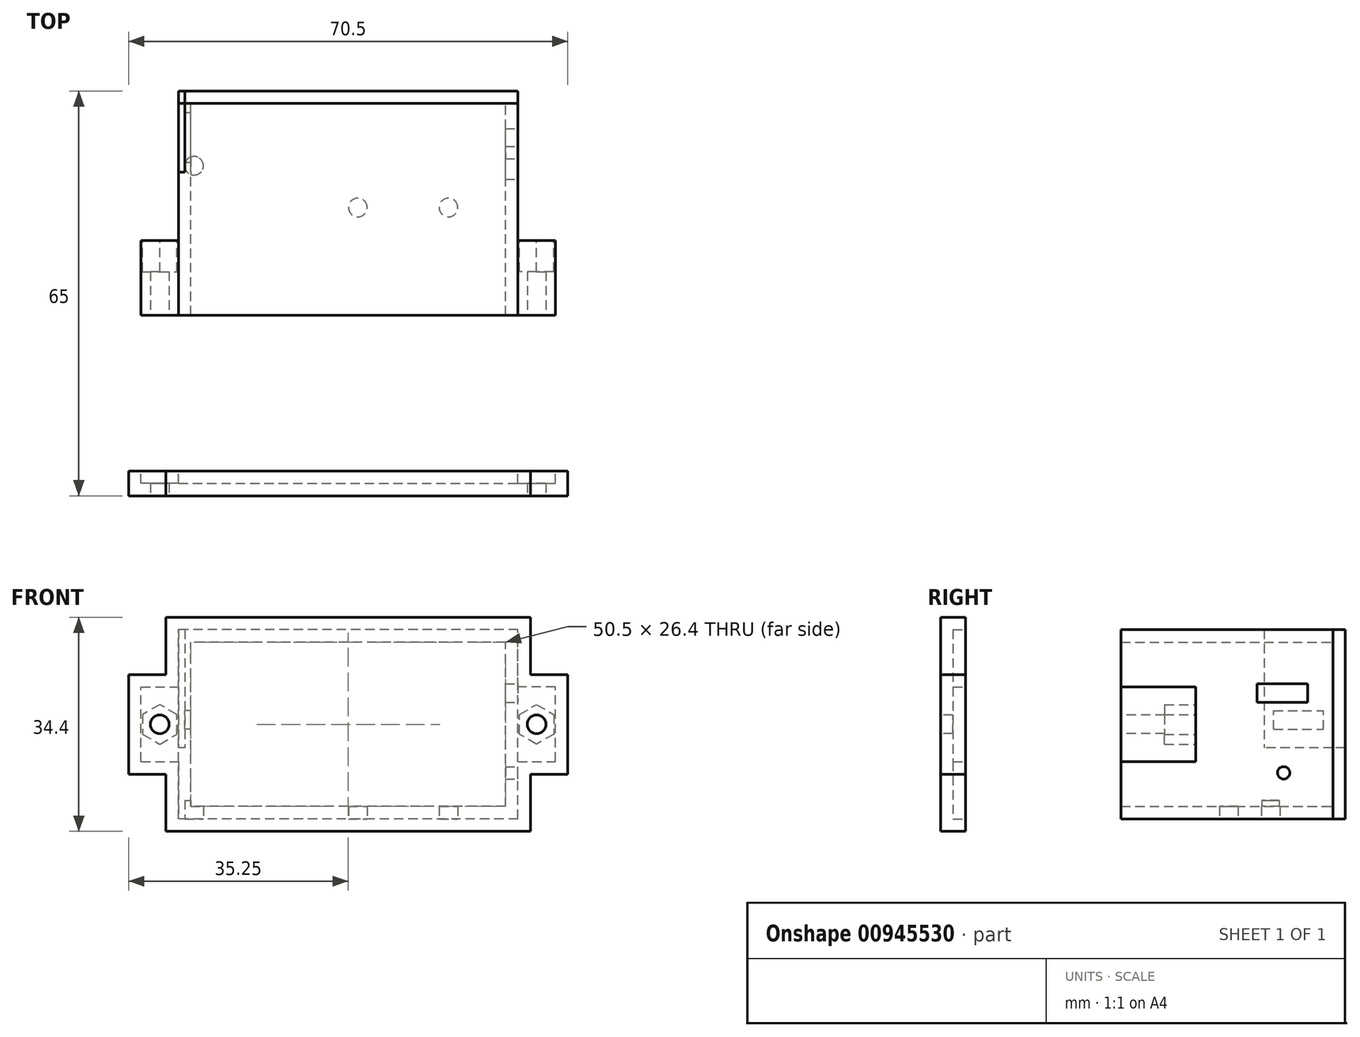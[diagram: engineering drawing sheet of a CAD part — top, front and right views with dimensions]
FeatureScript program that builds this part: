
annotation { "Feature Type Name" : "Feature", "Feature Type Description" : "" }
export const myFeature = defineFeature(function(context is Context, id is Id, definition is map)
    precondition{}
    {
        {
            var Q0;
            Q0=qCreatedBy(makeId("Front.planeOp"),FACE);
            var sketch = newSketch(context, id + "F0", { "sketchPlane" : qUnion([Q0])});
            skLineSegment(sketch, "E0.bottom", {"start": v(27.25, -15.2) * mm, "end": v(-27.25, -15.2) * mm});
            skLineSegment(sketch, "E0.top", {"start": v(27.25, 15.2) * mm, "end": v(-27.25, 15.2) * mm});
            skLineSegment(sketch, "E0.left", {"start": v(27.25, -15.2) * mm, "end": v(27.25, 15.2) * mm});
            skLineSegment(sketch, "E0.right", {"start": v(-27.25, -15.2) * mm, "end": v(-27.25, 15.2) * mm});
            skPoint(sketch, "E0.middle", {"position": v(0, 0) * mm});
            skLineSegment(sketch, "E1.bottom", {"start": v(25.25, -13.2) * mm, "end": v(-25.25, -13.2) * mm});
            skLineSegment(sketch, "E1.top", {"start": v(25.25, 13.2) * mm, "end": v(-25.25, 13.2) * mm});
            skLineSegment(sketch, "E1.left", {"start": v(25.25, -13.2) * mm, "end": v(25.25, 13.2) * mm});
            skLineSegment(sketch, "E1.right", {"start": v(-25.25, -13.2) * mm, "end": v(-25.25, 13.2) * mm});
            skSolve(sketch);
        }
        {
            var Q0;
            Q0=qSketchRegion(id+"F0",true);
            extrude(context, id + "F1", {"entities" : qUnion([Q0]), "depth" : 34 * mm, "offsetDistance" : 25 * mm});
        }
        {
            var Q0;
            Q0=makeQuery(id+"F1.opExtrude","CAP_FACE",FACE,{"disambiguationData":[OSD([sQuery(id+"F0.wireOp",EDGE,"E0.bottom"),sQuery(id+"F0.wireOp",EDGE,"E0.top"),sQuery(id+"F0.wireOp",EDGE,"E0.left"),sQuery(id+"F0.wireOp",EDGE,"E0.right"),sQuery(id+"F0.wireOp",EDGE,"E1.bottom"),sQuery(id+"F0.wireOp",EDGE,"E1.top"),sQuery(id+"F0.wireOp",EDGE,"E1.left"),sQuery(id+"F0.wireOp",EDGE,"E1.right")])],"isStart":true});
            var sketch = newSketch(context, id + "F2", { "sketchPlane" : qUnion([Q0])});
            skLineSegment(sketch, "E2.0.0", {"start": v(-27.25, 15.2) * mm, "end": v(-27.25, -15.2) * mm});
            skLineSegment(sketch, "E2.0.1", {"start": v(-27.25, -15.2) * mm, "end": v(27.25, -15.2) * mm});
            skLineSegment(sketch, "E2.0.2", {"start": v(27.25, -15.2) * mm, "end": v(27.25, 15.2) * mm});
            skLineSegment(sketch, "E2.0.3", {"start": v(27.25, 15.2) * mm, "end": v(-27.25, 15.2) * mm});
            skSolve(sketch);
        }
        {
            var Q0;
            Q0=qSketchRegion(id+"F2",true);
            extrude(context, id + "F3", {"entities" : qUnion([Q0]), "depth" : 2 * mm, "offsetDistance" : 25 * mm});
        }
        {
            var Q0;
            Q0=makeQuery(id+"F1.opExtrude","SWEPT_FACE",FACE,{"disambiguationData":[OSD([sQuery(id+"F0.wireOp",EDGE,"E0.right")])]});
            var sketch = newSketch(context, id + "F4", { "sketchPlane" : qUnion([Q0])});
            skLineSegment(sketch, "E3.bottom", {"start": v(22, -6) * mm, "end": v(34, -6) * mm});
            skLineSegment(sketch, "E3.top", {"start": v(22, 6) * mm, "end": v(34, 6) * mm});
            skLineSegment(sketch, "E3.left", {"start": v(22, -6) * mm, "end": v(22, 6) * mm});
            skLineSegment(sketch, "E3.right", {"start": v(34, -6) * mm, "end": v(34, 6) * mm});
            skPoint(sketch, "E3.middle", {"position": v(28, 0) * mm});
            skPoint(sketch, "E4.orphan", {"position": v(34, 15.2) * mm});
            skPoint(sketch, "E5.orphan", {"position": v(34, -15.2) * mm});
            skSolve(sketch);
        }
        {
            var Q0;
            Q0=qSketchRegion(id+"F4",true);
            extrude(context, id + "F5", {"entities" : qUnion([Q0]), "depth" : 6 * mm, "offsetDistance" : 25 * mm});
        }
        {
            var Q0;
            Q0=makeQuery(id+"F5.opExtrude","SWEPT_FACE",FACE,{"disambiguationData":[OSD([sQuery(id+"F4.wireOp",EDGE,"E3.right")])]});
            var sketch = newSketch(context, id + "F6", { "sketchPlane" : qUnion([Q0])});
            skLineSegment(sketch, "E6.0.0", {"start": v(-27.25, -6) * mm, "end": v(-27.25, 6) * mm, "construction": true});
            skLineSegment(sketch, "E6.0.1", {"start": v(-27.25, 6) * mm, "end": v(-33.25, 6) * mm, "construction": true});
            skLineSegment(sketch, "E6.0.2", {"start": v(-33.25, 6) * mm, "end": v(-33.25, -6) * mm, "construction": true});
            skLineSegment(sketch, "E6.0.3", {"start": v(-33.25, -6) * mm, "end": v(-27.25, -6) * mm, "construction": true});
            skCircle(sketch, "E7", {"center": v(-30.25, 0) * mm, "radius": 1.5 * mm});
            skPoint(sketch, "E7.centerSnap0", {"position": v(-27.25, 0) * mm});
            skSolve(sketch);
        }
        {
            var Q0;
            Q0=qSketchRegion(id+"F6",true);
            extrude(context, id + "F7", {"entities" : qUnion([Q0]), "operationType" : NewBodyOperationType.REMOVE, "oppositeDirection" : true, "depth" : 15 * mm, "offsetDistance" : 25 * mm});
        }
        {
            var Q0;
            Q0=makeQuery(id+"F5.opExtrude","SWEPT_FACE",FACE,{"disambiguationData":[OSD([sQuery(id+"F4.wireOp",EDGE,"E3.left")])]});
            var sketch = newSketch(context, id + "F8", { "sketchPlane" : qUnion([Q0])});
            skCircle(sketch, "E8.0", {"center": v(30.25, 0) * mm, "radius": 1.5 * mm});
            skCircle(sketch, "E9.cCircle", {"center": v(30.25, 0) * mm, "radius": 2.75 * mm, "construction": true});
            skLineSegment(sketch, "E9.0", {"start": v(30.25, -3.18) * mm, "end": v(27.5, -1.59) * mm});
            skLineSegment(sketch, "E9.1", {"start": v(27.5, -1.59) * mm, "end": v(27.5, 1.59) * mm});
            skLineSegment(sketch, "E9.2", {"start": v(27.5, 1.59) * mm, "end": v(30.25, 3.18) * mm});
            skLineSegment(sketch, "E9.3", {"start": v(30.25, 3.18) * mm, "end": v(33, 1.59) * mm});
            skLineSegment(sketch, "E9.4", {"start": v(33, 1.59) * mm, "end": v(33, -1.59) * mm});
            skLineSegment(sketch, "E9.5", {"start": v(33, -1.59) * mm, "end": v(30.25, -3.18) * mm});
            skPoint(sketch, "E9.0.midPoint", {"position": v(28.88, -2.38) * mm});
            skSolve(sketch);
        }
        {
            var Q0;
            Q0=qSketchRegion(id+"F8",true);
            extrude(context, id + "F9", {"entities" : qUnion([Q0]), "operationType" : NewBodyOperationType.REMOVE, "oppositeDirection" : true, "depth" : 5 * mm, "offsetDistance" : 25 * mm});
        }
        {
            var Q0;
            Q0=makeQuery(id+"F5.opExtrude","SWEPT_BODY",BODY,{"disambiguationData":[OSD([sQuery(id+"F4.wireOp",EDGE,"E3.bottom"),sQuery(id+"F4.wireOp",EDGE,"E3.top"),sQuery(id+"F4.wireOp",EDGE,"E3.left"),sQuery(id+"F4.wireOp",EDGE,"E3.right")])]});
            var Q1;
            Q1=qCreatedBy(makeId("Right.planeOp"),FACE);
            mirror(context, id + "F10", {"entities" : qUnion([Q0]), "mirrorPlane" : qUnion([Q1])});
        }
        {
            var Q0;
            Q0=makeQuery(id+"F1.opExtrude","CAP_FACE",FACE,{"disambiguationData":[OSD([sQuery(id+"F0.wireOp",EDGE,"E0.bottom"),sQuery(id+"F0.wireOp",EDGE,"E0.top"),sQuery(id+"F0.wireOp",EDGE,"E0.left"),sQuery(id+"F0.wireOp",EDGE,"E0.right"),sQuery(id+"F0.wireOp",EDGE,"E1.bottom"),sQuery(id+"F0.wireOp",EDGE,"E1.top"),sQuery(id+"F0.wireOp",EDGE,"E1.left"),sQuery(id+"F0.wireOp",EDGE,"E1.right")])],"isStart":false});
            cPlane(context, id + "F11", {"entities" : qUnion([Q0]), "cplaneType" : CPlaneType.OFFSET, "offset" : 25 * mm, "width" : 150 * mm, "height" : 150 * mm});
        }
        {
            var Q0;
            Q0=qCreatedBy(id+"F11.planeOp",FACE);
            var sketch = newSketch(context, id + "F12", { "sketchPlane" : qUnion([Q0])});
            skLineSegment(sketch, "E10.0.0", {"start": v(27.25, -15.2) * mm, "end": v(27.25, -6) * mm});
            skLineSegment(sketch, "E10.0.1", {"start": v(27.25, 15.2) * mm, "end": v(-27.25, 15.2) * mm});
            skLineSegment(sketch, "E10.0.2", {"start": v(-27.25, 15.2) * mm, "end": v(-27.25, 6) * mm});
            skLineSegment(sketch, "E10.0.3", {"start": v(-27.25, -15.2) * mm, "end": v(27.25, -15.2) * mm});
            skLineSegment(sketch, "E11.0.1", {"start": v(-27.25, 6) * mm, "end": v(-33.25, 6) * mm});
            skLineSegment(sketch, "E11.0.2", {"start": v(-33.25, 6) * mm, "end": v(-33.25, -6) * mm});
            skLineSegment(sketch, "E11.0.3", {"start": v(-33.25, -6) * mm, "end": v(-27.25, -6) * mm});
            skLineSegment(sketch, "E12.0.1", {"start": v(27.25, -6) * mm, "end": v(33.25, -6) * mm});
            skLineSegment(sketch, "E12.0.2", {"start": v(33.25, -6) * mm, "end": v(33.25, 6) * mm});
            skLineSegment(sketch, "E12.0.3", {"start": v(33.25, 6) * mm, "end": v(27.25, 6) * mm});
            skLineSegment(sketch, "E13.trimOffspring", {"start": v(-27.25, -6) * mm, "end": v(-27.25, -15.2) * mm});
            skLineSegment(sketch, "E14.trimOffspring", {"start": v(27.25, 6) * mm, "end": v(27.25, 15.2) * mm});
            skSolve(sketch);
        }
        {
            var Q0;
            Q0=qSketchRegion(id+"F12",true);
            extrude(context, id + "F13", {"entities" : qUnion([Q0]), "depth" : 2 * mm, "offsetDistance" : 25 * mm});
        }
        {
            var Q0;
            Q0=makeQuery(id+"F13.opExtrude","CAP_FACE",FACE,{"disambiguationData":[OSD([sQuery(id+"F12.wireOp",EDGE,"E10.0.0"),sQuery(id+"F12.wireOp",EDGE,"E10.0.1"),sQuery(id+"F12.wireOp",EDGE,"E10.0.2"),sQuery(id+"F12.wireOp",EDGE,"E10.0.3"),sQuery(id+"F12.wireOp",EDGE,"E11.0.1"),sQuery(id+"F12.wireOp",EDGE,"E11.0.2"),sQuery(id+"F12.wireOp",EDGE,"E11.0.3"),sQuery(id+"F12.wireOp",EDGE,"E12.0.1"),sQuery(id+"F12.wireOp",EDGE,"E12.0.2"),sQuery(id+"F12.wireOp",EDGE,"E12.0.3"),sQuery(id+"F12.wireOp",EDGE,"64ac5859-c408-4472-a5fe-9f76c2f57aa8.0"),sQuery(id+"F12.wireOp",EDGE,"51b21d13-924f-4e29-874b-db9c67d27de5.0"),sQuery(id+"F12.wireOp",EDGE,"E13.trimOffspring"),sQuery(id+"F12.wireOp",EDGE,"E14.trimOffspring")])],"isStart":true});
            shell(context, id + "F14", {"entities" : qUnion([Q0]), "thickness" : 2 * mm, "oppositeDirection" : true});
        }
        {
            var Q0;
            Q0=makeQuery(id+"F13.opExtrude","CAP_FACE",FACE,{"disambiguationData":[OSD([sQuery(id+"F12.wireOp",EDGE,"E10.0.0"),sQuery(id+"F12.wireOp",EDGE,"E10.0.1"),sQuery(id+"F12.wireOp",EDGE,"E10.0.2"),sQuery(id+"F12.wireOp",EDGE,"E10.0.3"),sQuery(id+"F12.wireOp",EDGE,"E11.0.1"),sQuery(id+"F12.wireOp",EDGE,"E11.0.2"),sQuery(id+"F12.wireOp",EDGE,"E11.0.3"),sQuery(id+"F12.wireOp",EDGE,"E12.0.1"),sQuery(id+"F12.wireOp",EDGE,"E12.0.2"),sQuery(id+"F12.wireOp",EDGE,"E12.0.3"),sQuery(id+"F12.wireOp",EDGE,"E13.trimOffspring"),sQuery(id+"F12.wireOp",EDGE,"E14.trimOffspring")])],"isStart":false});
            var sketch = newSketch(context, id + "F15", { "sketchPlane" : qUnion([Q0])});
            skCircle(sketch, "E15.0", {"center": v(-30.25, 0) * mm, "radius": 1.5 * mm});
            skCircle(sketch, "E16.0", {"center": v(30.25, 0) * mm, "radius": 1.5 * mm});
            skSolve(sketch);
        }
        {
            var Q0;
            Q0=qSketchRegion(id+"F15",true);
            extrude(context, id + "F16", {"entities" : qUnion([Q0]), "operationType" : NewBodyOperationType.REMOVE, "oppositeDirection" : true, "depth" : 3 * mm, "offsetDistance" : 25 * mm});
        }
        {
            var Q0;
            Q0=makeQuery(id+"F1.opExtrude","SWEPT_FACE",FACE,{"disambiguationData":[OSD([sQuery(id+"F0.wireOp",EDGE,"E0.bottom")])]});
            var sketch = newSketch(context, id + "F17", { "sketchPlane" : qUnion([Q0])});
            skLineSegment(sketch, "E17.0.0", {"start": v(-27.25, 0) * mm, "end": v(27.25, 0) * mm, "construction": true});
            skLineSegment(sketch, "E17.0.1", {"start": v(27.25, 0) * mm, "end": v(27.25, 34) * mm, "construction": true});
            skLineSegment(sketch, "E17.0.2", {"start": v(27.25, 34) * mm, "end": v(-27.25, 34) * mm, "construction": true});
            skLineSegment(sketch, "E17.0.3", {"start": v(-27.25, 34) * mm, "end": v(-27.25, 0) * mm, "construction": true});
            skCircle(sketch, "E18", {"center": v(16.1, 16.7) * mm, "radius": 1.5 * mm});
            skCircle(sketch, "E19", {"center": v(1.55, 16.7) * mm, "radius": 1.5 * mm});
            skCircle(sketch, "E20", {"center": v(-24.75, 10) * mm, "radius": 1.5 * mm});
            skSolve(sketch);
        }
        {
            var Q0;
            Q0=qSketchRegion(id+"F17",true);
            extrude(context, id + "F18", {"entities" : qUnion([Q0]), "operationType" : NewBodyOperationType.REMOVE, "oppositeDirection" : true, "depth" : 3 * mm, "offsetDistance" : 25 * mm});
        }
        {
            var Q0;
            Q0=makeQuery(id+"F1.opExtrude","SWEPT_FACE",FACE,{"disambiguationData":[OSD([sQuery(id+"F0.wireOp",EDGE,"E0.right")])]});
            var sketch = newSketch(context, id + "F19", { "sketchPlane" : qUnion([Q0])});
            skLineSegment(sketch, "E21.0.1", {"start": v(0, -15.2) * mm, "end": v(34, -15.2) * mm, "construction": true});
            skLineSegment(sketch, "E21.0.2", {"start": v(34, -15.2) * mm, "end": v(34, 15.2) * mm, "construction": true});
            skLineSegment(sketch, "E21.0.3", {"start": v(34, 15.2) * mm, "end": v(-2, 15.2) * mm, "construction": true});
            skLineSegment(sketch, "E22.bottom", {"start": v(-2, 15.2) * mm, "end": v(11, 15.2) * mm});
            skLineSegment(sketch, "E22.top", {"start": v(-2, -3.8) * mm, "end": v(11, -3.8) * mm});
            skLineSegment(sketch, "E22.left", {"start": v(-2, 15.2) * mm, "end": v(-2, -3.8) * mm});
            skLineSegment(sketch, "E22.right", {"start": v(11, 15.2) * mm, "end": v(11, -3.8) * mm});
            skPoint(sketch, "E23.0", {"position": v(-2, 15.2) * mm});
            skSolve(sketch);
        }
        {
            var Q0;
            Q0=qSketchRegion(id+"F19",true);
            extrude(context, id + "F20", {"entities" : qUnion([Q0]), "operationType" : NewBodyOperationType.REMOVE, "oppositeDirection" : true, "depth" : 1 * mm, "offsetDistance" : 25 * mm});
        }
        {
            var Q0;
            Q0=makeQuery(id+"F1.opExtrude","SWEPT_FACE",FACE,{"disambiguationData":[OSD([sQuery(id+"F0.wireOp",EDGE,"E0.left")])]});
            var sketch = newSketch(context, id + "F21", { "sketchPlane" : qUnion([Q0])});
            skLineSegment(sketch, "E24.0.0", {"start": v(0, -15.2) * mm, "end": v(0, 15.2) * mm});
            skLineSegment(sketch, "E24.0.1", {"start": v(0, 15.2) * mm, "end": v(-34, 15.2) * mm});
            skLineSegment(sketch, "E24.0.2", {"start": v(-34, 15.2) * mm, "end": v(-34, -15.2) * mm});
            skLineSegment(sketch, "E24.0.3", {"start": v(-34, -15.2) * mm, "end": v(0, -15.2) * mm});
            skLineSegment(sketch, "E25.bottom", {"start": v(-4.05, 6.5) * mm, "end": v(-12.15, 6.5) * mm});
            skLineSegment(sketch, "E25.top", {"start": v(-4.05, 3.54) * mm, "end": v(-12.15, 3.54) * mm});
            skLineSegment(sketch, "E25.left", {"start": v(-4.05, 6.5) * mm, "end": v(-4.05, 3.54) * mm});
            skLineSegment(sketch, "E25.right", {"start": v(-12.15, 6.5) * mm, "end": v(-12.15, 3.54) * mm});
            skSolve(sketch);
        }
        {
            var Q0;
            Q0=makeQuery(id+"F21.imprint","IMPRINT",FACE,{"disambiguationData":[TD([[makeQuery(id+"F21.imprint","IMPRINT",EDGE,{"derivedFrom":sQuery(id+"F21.wireOp",EDGE,"E25.bottom")}),1.0]])]});
            var sketch = newSketch(context, id + "F22", { "sketchPlane" : qUnion([Q0])});
            skPoint(sketch, "E26.0", {"position": v(-8.1, 3.54) * mm});
            skPoint(sketch, "E27.0", {"position": v(-4.05, 3.54) * mm});
            skPoint(sketch, "E28.0", {"position": v(-4.05, 6.5) * mm});
            skPoint(sketch, "E29.0", {"position": v(-12.15, 6.5) * mm});
            skPoint(sketch, "E30.0", {"position": v(-12.15, 3.54) * mm});
            skLineSegment(sketch, "E31.0.0", {"start": v(-12.15, 3.54) * mm, "end": v(-4.05, 3.54) * mm});
            skLineSegment(sketch, "E31.0.1", {"start": v(-4.05, 3.54) * mm, "end": v(-4.05, 6.5) * mm});
            skLineSegment(sketch, "E31.0.2", {"start": v(-4.05, 6.5) * mm, "end": v(-12.15, 6.5) * mm});
            skLineSegment(sketch, "E31.0.3", {"start": v(-12.15, 6.5) * mm, "end": v(-12.15, 3.54) * mm});
            skSolve(sketch);
        }
        {
            var Q0;
            Q0=qSketchRegion(id+"F22",true);
            extrude(context, id + "F23", {"entities" : qUnion([Q0]), "operationType" : NewBodyOperationType.REMOVE, "oppositeDirection" : true, "depth" : 5 * mm, "offsetDistance" : 25 * mm});
        }
        {
            var Q0;
            Q0=makeQuery(id+"F21.imprint","IMPRINT",FACE,{"disambiguationData":[TD([[makeQuery(id+"F21.imprint","IMPRINT",EDGE,{"derivedFrom":sQuery(id+"F21.wireOp",EDGE,"E24.0.0")}),1.0]])]});
            var sketch = newSketch(context, id + "F24", { "sketchPlane" : qUnion([Q0])});
            skCircle(sketch, "E32", {"center": v(-7.89, -7.8) * mm, "radius": 1 * mm});
            skSolve(sketch);
        }
        {
            var Q0;
            Q0=qSketchRegion(id+"F24",true);
            extrude(context, id + "F25", {"entities" : qUnion([Q0]), "operationType" : NewBodyOperationType.REMOVE, "oppositeDirection" : true, "depth" : 5 * mm, "offsetDistance" : 25 * mm});
        }
        {
            var Q0;
            {var subQ0=sQuery(id+"F0.wireOp",EDGE,"E0.top");var subQ1=sQuery(id+"F19.wireOp",EDGE,"E22.right");var subQ2=sQuery(id+"F19.wireOp",EDGE,"E22.top");Q0=makeQuery(id+"F20.boolean.opBoolean","COPY",FACE,{"disambiguationData":[TD([makeQuery(id+"F1.opExtrude","SWEPT_FACE",FACE,{"disambiguationData":[OSD([subQ0])]})])],"derivedFrom":makeQuery(id+"F20.opExtrude","CAP_FACE",FACE,{"disambiguationData":[OSD([sQuery(id+"F19.wireOp",EDGE,"E22.bottom"),subQ2,sQuery(id+"F19.wireOp",EDGE,"E22.left"),subQ1])],"isStart":false})});}
            var sketch = newSketch(context, id + "F26", { "sketchPlane" : qUnion([Q0])});
            skLineSegment(sketch, "E33.bottom", {"start": v(9.5, -0.8) * mm, "end": v(1.5, -0.8) * mm});
            skLineSegment(sketch, "E33.top", {"start": v(9.5, 2.2) * mm, "end": v(1.5, 2.2) * mm});
            skLineSegment(sketch, "E33.left", {"start": v(9.5, -0.8) * mm, "end": v(9.5, 2.2) * mm});
            skLineSegment(sketch, "E33.right", {"start": v(1.5, -0.8) * mm, "end": v(1.5, 2.2) * mm});
            skSolve(sketch);
        }
        {
            var Q0;
            Q0=makeQuery(id+"F26.imprint","IMPRINT",FACE,{"disambiguationData":[TD([[makeQuery(id+"F26.imprint","IMPRINT",EDGE,{"derivedFrom":sQuery(id+"F26.wireOp",EDGE,"E33.bottom")}),-1.0]])]});
            extrude(context, id + "F27", {"entities" : qUnion([Q0]), "operationType" : NewBodyOperationType.REMOVE, "oppositeDirection" : true, "depth" : 5 * mm, "offsetDistance" : 25 * mm});
        }
    });
